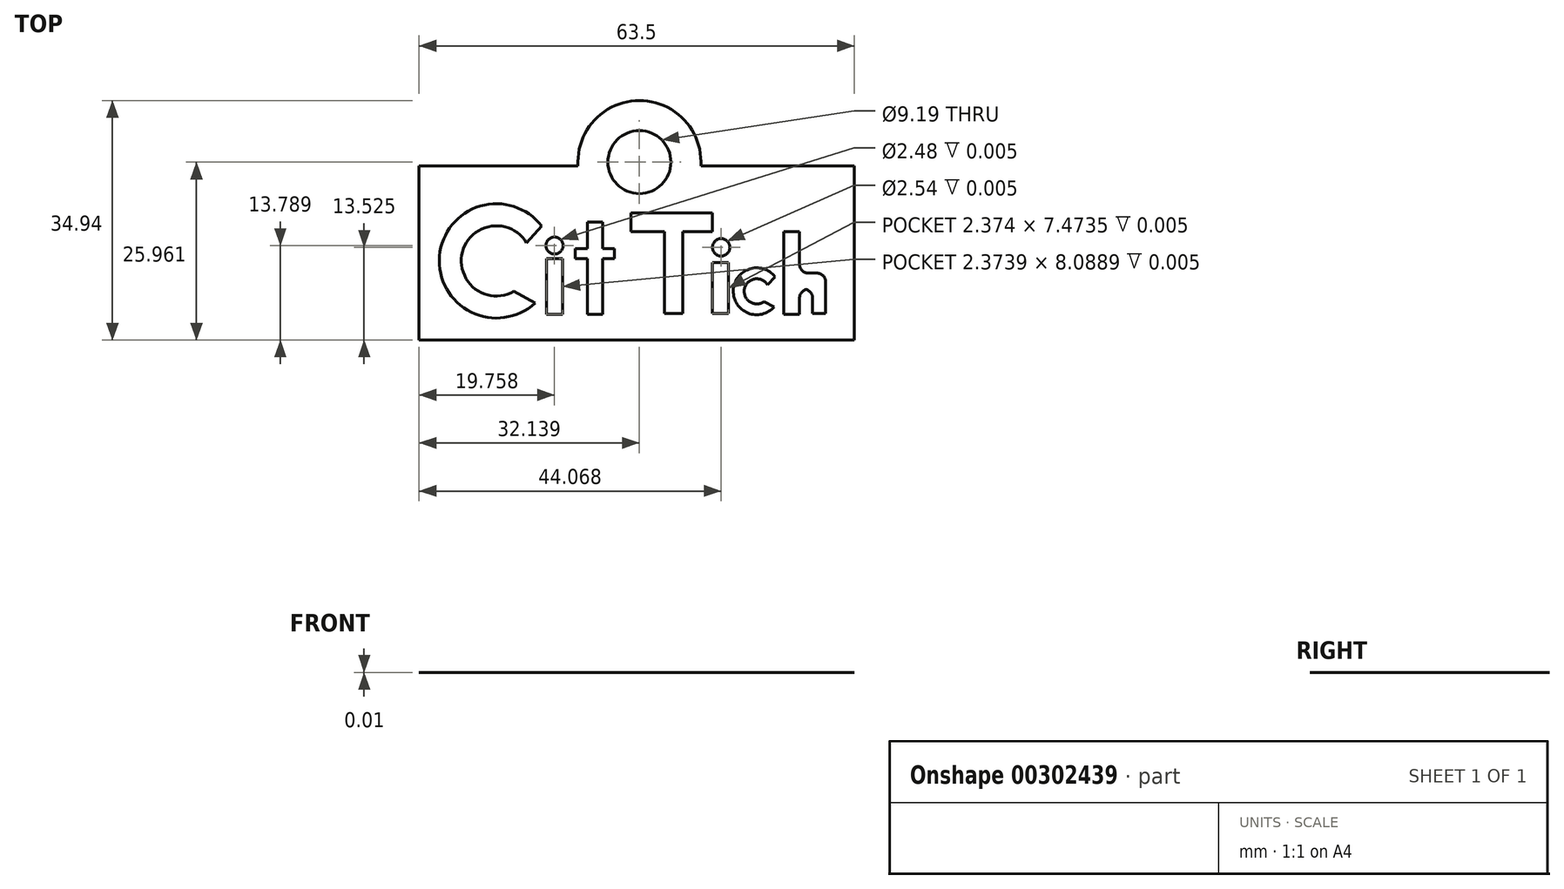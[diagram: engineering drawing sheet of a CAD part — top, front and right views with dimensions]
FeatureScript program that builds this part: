
annotation { "Feature Type Name" : "Feature", "Feature Type Description" : "" }
export const myFeature = defineFeature(function(context is Context, id is Id, definition is map)
    precondition{}
    {
        {
            var Q0;
            Q0=qCreatedBy(makeId("Top.planeOp"),FACE);
            var sketch = newSketch(context, id + "F0", { "sketchPlane" : qUnion([Q0])});
            skLineSegment(sketch, "E0.bottom", {"start": v(0, 0) * mm, "end": v(-63.5, 0) * mm});
            skLineSegment(sketch, "E0.top", {"start": v(0, 25.4) * mm, "end": v(-22.4, 25.4) * mm});
            skLineSegment(sketch, "E0.left", {"start": v(0, 0) * mm, "end": v(0, 25.4) * mm});
            skLineSegment(sketch, "E0.right", {"start": v(-63.5, 0) * mm, "end": v(-63.5, 25.4) * mm});
            skArc(sketch, "E1", {"start": v(-22.4, 25.4) * mm, "mid": v(-31.36, 34.94) * mm, "end": v(-40.32, 25.4) * mm});
            skCircle(sketch, "E2", {"center": v(-31.36, 25.96) * mm, "radius": 4.6 * mm});
            skLineSegment(sketch, "E3.trimOffspring", {"start": v(-40.32, 25.4) * mm, "end": v(-63.5, 25.4) * mm});
            skSolve(sketch);
        }
        {
            var Q0;
            Q0=makeQuery(id+"F0.imprint","IMPRINT",FACE,{"disambiguationData":[TD([[makeQuery(id+"F0.imprint","IMPRINT",EDGE,{"derivedFrom":sQuery(id+"F0.wireOp",EDGE,"E0.bottom")}),-1.0]])]});
            extrude(context, id + "F1", {"entities" : qUnion([Q0]), "depth" : 1 / 101.6 * mm});
        }
        {
            var Q0;
            Q0=makeQuery(id+"F1.opExtrude","CAP_FACE",FACE,{"disambiguationData":[OSD([sQuery(id+"F0.wireOp",EDGE,"E0.bottom"),sQuery(id+"F0.wireOp",EDGE,"E0.top"),sQuery(id+"F0.wireOp",EDGE,"E0.left"),sQuery(id+"F0.wireOp",EDGE,"E0.right"),sQuery(id+"F0.wireOp",EDGE,"E1"),sQuery(id+"F0.wireOp",EDGE,"E2"),sQuery(id+"F0.wireOp",EDGE,"E3.trimOffspring")])],"isStart":false});
            var sketch = newSketch(context, id + "F2", { "sketchPlane" : qUnion([Q0])});
            skArc(sketch, "E4", {"start": v(-45.63, 16.66) * mm, "mid": v(-60.52, 12.26) * mm, "end": v(-46.6, 5.39) * mm});
            skArc(sketch, "E5", {"start": v(-47.81, 14.17) * mm, "mid": v(-57.17, 12.85) * mm, "end": v(-49.67, 7.1) * mm});
            skLineSegment(sketch, "E6", {"start": v(-47.81, 14.17) * mm, "end": v(-45.63, 16.66) * mm});
            skLineSegment(sketch, "E7", {"start": v(-49.67, 7.1) * mm, "end": v(-46.6, 5.39) * mm});
            skLineSegment(sketch, "E8.bottom", {"start": v(-32.62, 18.54) * mm, "end": v(-20.75, 18.54) * mm});
            skLineSegment(sketch, "E8.top", {"start": v(-32.62, 15.78) * mm, "end": v(-27.7, 15.78) * mm});
            skLineSegment(sketch, "E8.left", {"start": v(-32.62, 18.54) * mm, "end": v(-32.62, 15.78) * mm});
            skLineSegment(sketch, "E8.right", {"start": v(-20.75, 18.54) * mm, "end": v(-20.75, 15.78) * mm});
            skLineSegment(sketch, "E9.top", {"start": v(-27.7, 3.85) * mm, "end": v(-25.06, 3.85) * mm});
            skLineSegment(sketch, "E9.left", {"start": v(-27.7, 15.78) * mm, "end": v(-27.7, 3.85) * mm});
            skLineSegment(sketch, "E9.right", {"start": v(-25.06, 15.81) * mm, "end": v(-25.06, 3.85) * mm});
            skLineSegment(sketch, "E10.bottom", {"start": v(-20.75, 11.33) * mm, "end": v(-18.38, 11.33) * mm});
            skLineSegment(sketch, "E10.top", {"start": v(-20.75, 3.85) * mm, "end": v(-18.38, 3.85) * mm});
            skLineSegment(sketch, "E10.left", {"start": v(-20.75, 11.33) * mm, "end": v(-20.75, 3.85) * mm});
            skLineSegment(sketch, "E10.right", {"start": v(-18.38, 11.33) * mm, "end": v(-18.38, 3.85) * mm});
            skLineSegment(sketch, "E11.bottom", {"start": v(-10.29, 15.78) * mm, "end": v(-8, 15.78) * mm});
            skLineSegment(sketch, "E11.top", {"start": v(-10.29, 3.77) * mm, "end": v(-8, 3.77) * mm});
            skLineSegment(sketch, "E11.left", {"start": v(-10.29, 15.78) * mm, "end": v(-10.29, 3.77) * mm});
            skLineSegment(sketch, "E11.right", {"start": v(-8, 15.78) * mm, "end": v(-8, 11.05) * mm});
            skPoint(sketch, "E12.oppositeSnap0", {"position": v(-9.14, 3.77) * mm});
            skLineSegment(sketch, "E12.bottom", {"start": v(-44.93, 11.85) * mm, "end": v(-42.56, 11.85) * mm});
            skLineSegment(sketch, "E12.top", {"start": v(-44.93, 3.77) * mm, "end": v(-42.56, 3.77) * mm});
            skLineSegment(sketch, "E12.left", {"start": v(-44.93, 11.85) * mm, "end": v(-44.93, 3.77) * mm});
            skLineSegment(sketch, "E12.right", {"start": v(-42.56, 11.85) * mm, "end": v(-42.56, 3.77) * mm});
            skLineSegment(sketch, "E13.bottom", {"start": v(-38.95, 17.22) * mm, "end": v(-36.75, 17.22) * mm});
            skLineSegment(sketch, "E13.top", {"start": v(-38.95, 3.77) * mm, "end": v(-36.75, 3.77) * mm});
            skLineSegment(sketch, "E13.left", {"start": v(-38.95, 17.22) * mm, "end": v(-38.95, 13.35) * mm});
            skLineSegment(sketch, "E13.right", {"start": v(-36.75, 17.22) * mm, "end": v(-36.75, 13.35) * mm});
            skLineSegment(sketch, "E14.bottom", {"start": v(-40.7, 13.35) * mm, "end": v(-38.95, 13.35) * mm});
            skLineSegment(sketch, "E14.top", {"start": v(-40.7, 11.85) * mm, "end": v(-38.95, 11.85) * mm});
            skLineSegment(sketch, "E14.left", {"start": v(-40.7, 13.35) * mm, "end": v(-40.7, 11.85) * mm});
            skLineSegment(sketch, "E14.right", {"start": v(-35, 13.35) * mm, "end": v(-35, 11.85) * mm});
            skCircle(sketch, "E15", {"center": v(-19.43, 13.53) * mm, "radius": 1.27 * mm});
            skArc(sketch, "E16", {"start": v(-11.57, 9.24) * mm, "mid": v(-17.66, 7.2) * mm, "end": v(-11.7, 4.83) * mm});
            skArc(sketch, "E17", {"start": v(-12.68, 8.06) * mm, "mid": v(-16.04, 7.48) * mm, "end": v(-13.19, 5.61) * mm});
            skLineSegment(sketch, "E18", {"start": v(-12.68, 8.06) * mm, "end": v(-11.57, 9.24) * mm});
            skLineSegment(sketch, "E19", {"start": v(-13.19, 5.61) * mm, "end": v(-11.7, 4.83) * mm});
            skCircle(sketch, "E20", {"center": v(-43.74, 13.79) * mm, "radius": 1.24 * mm});
            skPoint(sketch, "E20.centerSnap0", {"position": v(-43.74, 11.85) * mm});
            skLineSegment(sketch, "E21.trimOffspring", {"start": v(-36.75, 13.35) * mm, "end": v(-35, 13.35) * mm});
            skLineSegment(sketch, "E22.trimOffspring", {"start": v(-36.75, 11.85) * mm, "end": v(-36.75, 3.77) * mm});
            skLineSegment(sketch, "E23.trimOffspring", {"start": v(-36.75, 11.85) * mm, "end": v(-35, 11.85) * mm});
            skLineSegment(sketch, "E24.trimOffspring", {"start": v(-38.95, 11.85) * mm, "end": v(-38.95, 3.77) * mm});
            skPoint(sketch, "E25.start.orphan", {"position": v(-10.29, 9.78) * mm});
            skLineSegment(sketch, "E26", {"start": v(-6.73, 9.78) * mm, "end": v(-5.47, 9.78) * mm});
            skLineSegment(sketch, "E27", {"start": v(-4.2, 8.5) * mm, "end": v(-4.2, 3.85) * mm});
            skLineSegment(sketch, "E28", {"start": v(-4.2, 3.85) * mm, "end": v(-6.1, 3.85) * mm});
            skLineSegment(sketch, "E29", {"start": v(-6.1, 3.85) * mm, "end": v(-6.1, 6.14) * mm});
            skLineSegment(sketch, "E30", {"start": v(-8, 3.77) * mm, "end": v(-8, 6.14) * mm});
            skLineSegment(sketch, "E31", {"start": v(-7.36, 7.41) * mm, "end": v(-6.73, 7.41) * mm});
            skPoint(sketch, "E32.visualSharp", {"position": v(-4.2, 9.78) * mm});
            skArc(sketch, "E32.filletArc", {"start": v(-4.2, 8.5) * mm, "mid": v(-4.57, 9.4) * mm, "end": v(-5.47, 9.78) * mm});
            skPoint(sketch, "E33.visualSharp", {"position": v(-6.1, 7.41) * mm});
            skArc(sketch, "E33.filletArc", {"start": v(-6.1, 6.14) * mm, "mid": v(-6.46, 7.04) * mm, "end": v(-7.36, 7.41) * mm});
            skPoint(sketch, "E34.visualSharp", {"position": v(-8, 7.41) * mm});
            skArc(sketch, "E34.filletArc", {"start": v(-6.73, 7.41) * mm, "mid": v(-7.63, 7.04) * mm, "end": v(-8, 6.14) * mm});
            skPoint(sketch, "E35.visualSharp", {"position": v(-8, 9.78) * mm});
            skArc(sketch, "E35.filletArc", {"start": v(-8, 11.05) * mm, "mid": v(-7.63, 10.15) * mm, "end": v(-6.73, 9.78) * mm});
            skLineSegment(sketch, "E36.trimOffspring", {"start": v(-25.06, 15.78) * mm, "end": v(-20.75, 15.78) * mm});
            skSolve(sketch);
        }
        {
            var Q0;
            Q0 = qSketchRegion(id + "F2", true);
            extrude(context, id + "F3", {"entities" : qUnion([Q0]), "operationType" : NewBodyOperationType.REMOVE, "oppositeDirection" : true, "depth" : 1 / 203.2 * mm});
        }
    });
